# Revit family: Atdec-Wall_Mount_Rail-VWP-
name_source: partatom
category: Generic Models
revit_build: Autodesk Revit 2016 (Build: 20150220_1215(x64)
units: mm (PartAtom-declared; Revit-internal decimal feet)

## family parameters
Can host rebar = No
Cut with Voids When Loaded = No
Host = Face
Part Type = Normal
Room Calculation Point = No
Round Connector Dimension = Use Diameter
Shared = No

## types (4) — shared parameters
Assembly Code = E1010800
Colour Options = Black
Default Elevation = 1219 mm
Flat screen maximum supported weight = 165kg (363lb)
Manufacturer = Atdec
Material = Steel
Maximum distance from wall (mm) = -
Minimum distance from wall (mm) = -
Pan Adjustment = -
Product Family = Wall Mount Rail
Product Information link = https://www.atdec.com.au
Range of Motion = -
Security feature = -
Tilt Adjustment = -
URL = www.atdec.com.au
Universal Height (mm) = -
Universal Width (mm) = -
VESA mounting hole pattern,mm = -
Warranty = 10 years

## per-type parameters (varying)
| type | Description | Master Carton Dimensions | Single Unit Dimensions | Single units per master pack | UPC Code | Weight, Master Carton | Weight, Single Unit | Width |
| TH-VWP-050 | Video wall 0.5m (19.6") mounting rail | 609mm (24") Lenght, 152mm (6") Width, 225mm (8.8") Height | 593mm (23.3") Lenght, 136mm (5.4") Width, 52mm (2") Height | 4 | 881493009486 | 7.5kg (16.5lb) | 1.8kg (3.9lb) | 500 mm  [stored 1.64042 ft] |
| TH-VWP-080 | Video wall 0.8m (31.4") mounting rail | 909mm (35.8") Lenght, 152mm (6") Width, 127mm (5") Height | 893mm (35.2") Lenght, 136mm (5.4") Width, 52mm (2") Height | 2 | 881493009509 | 6.4kg (14.1lb) | 3kg (6.6lb) | 800 mm  [stored 2.62467 ft] |
| TH-VWP-100 | Video wall 1m (39.3") mounting rail | 110mm (43.7") Lenght, 14.5mm (6.7") Width, 15mm (6.7") Height | 1078mm (42.9") Lenght, 118mm (5.9") Width, 55mm (3") Height | 2 | 881493008045 | 8kg (17.6lb) | 3.5kg (7.7lb) | 1000 mm  [stored 3.28084 ft] |
| TH-VWP-160 | Video wall 1.6m (62.9") mounting rail | 1687mm (67.3") Lenght, 133mm (6.7") Width, 142mm (6.7") Height | 1673mm (66.5") Lenght, 118mm (5.9") Width, 55mm (3") Height | 2 | 881493008120 | 12.5kg (27.5lb) | 6kg (13.2lb) | 1600 mm  [stored 5.24934 ft] |

note: column(s) folded — value = type name in every type: Model

note: [stored X ft] marks values corroborated as IEEE doubles in the binary element streams (Revit-internal decimal feet)

## geometry (parser evidence)
native form markers: Sweep x3
no freeform markers — native parametric forms only
